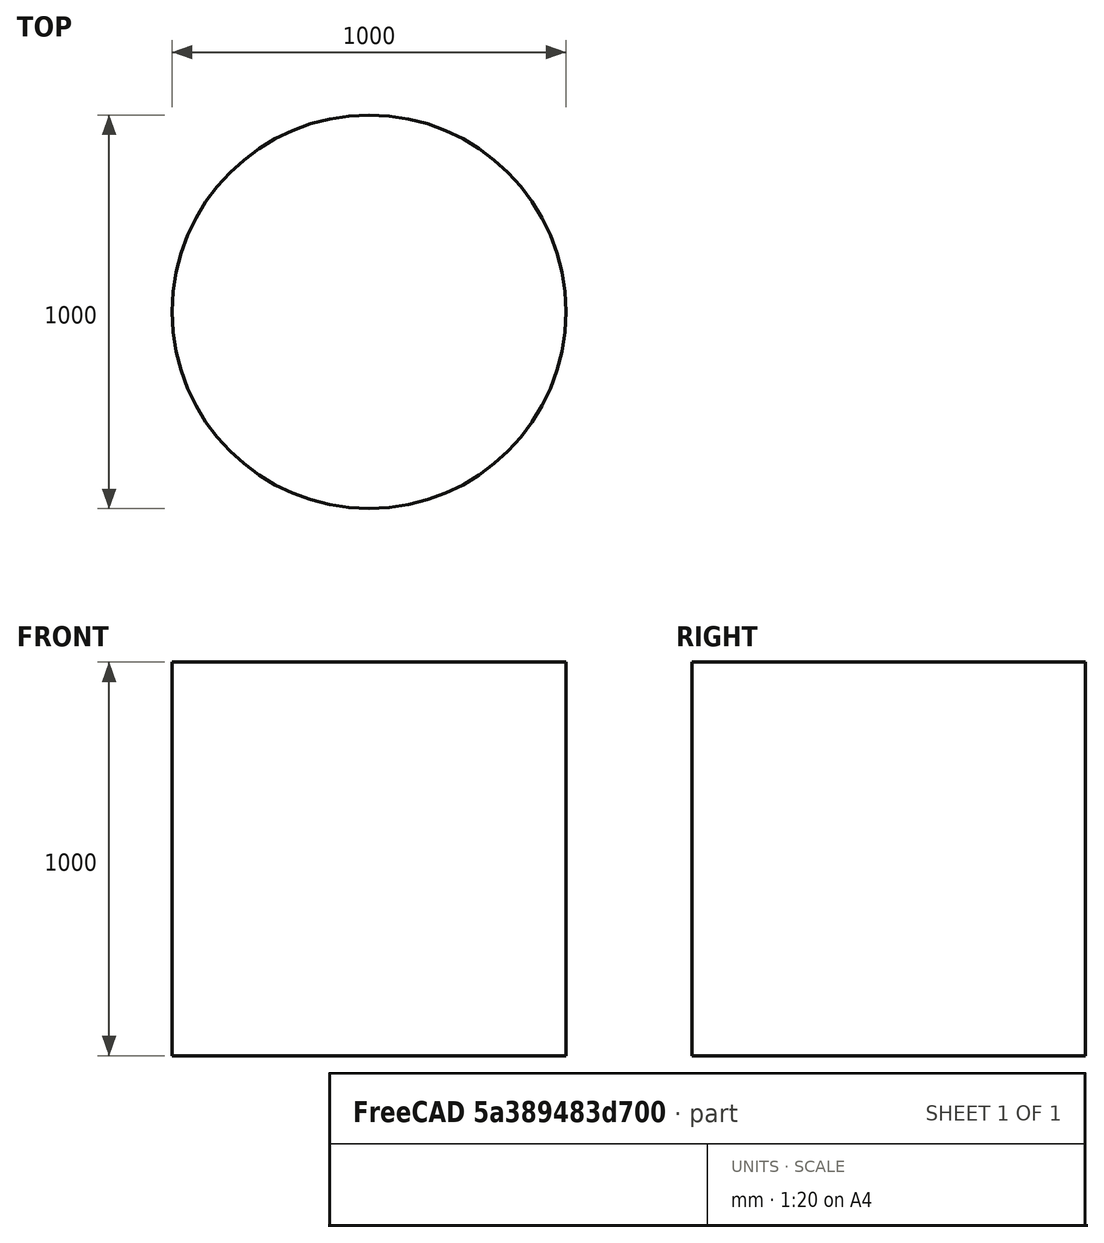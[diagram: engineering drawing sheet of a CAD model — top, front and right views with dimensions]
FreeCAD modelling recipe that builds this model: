
FCSTD DOCUMENT  (FreeCAD 1.0R39319 (Git))
Label: Cylinder-v1
License: All rights reserved
LicenseURL: https://en.wikipedia.org/wiki/All_rights_reserved
objects: Part::Cylinder×1, App::VarSet×1
note: 1 computed .brp shape members not serialized (recipe doc carries the construction recipe); baked Part::Feature solids carry a one-line shape summary decoded from their .brp

FEATURE [Part::Cylinder] Cylinder
  Angle = 360
  AttacherType = Attacher::AttachEngine3D
  FirstAngle = 0
  Height = 1000
  Radius = 500
  SecondAngle = 0
  expr: Height = <<PQs>>.Height
  expr: Radius = <<PQs>>.Dia / 2
FEATURE [App::VarSet] VarSet  label="PQs"
  CalcsLiveMappings = {\n  "docVersion": "0.2",\n  "unitsSchema": "UserPreferred",\n  "articleId": "3MBJZEAYJ-3YY",\n  "articleTitle": "Cylinder Calculation for FreeCAD Integration Demo",\n  "lastUpdated": "2025-11-08T05:40:17.230Z",\n  "pqMappings": {\n    "Dia": {\n      "symbol": "D",\n      "faceUnit": "m"\n    },\n    "Height": {\n      "symbol": "H",\n      "faceUnit": "m"\n    }\n  }\n}
  Dia = 1000
  Height = 1000
